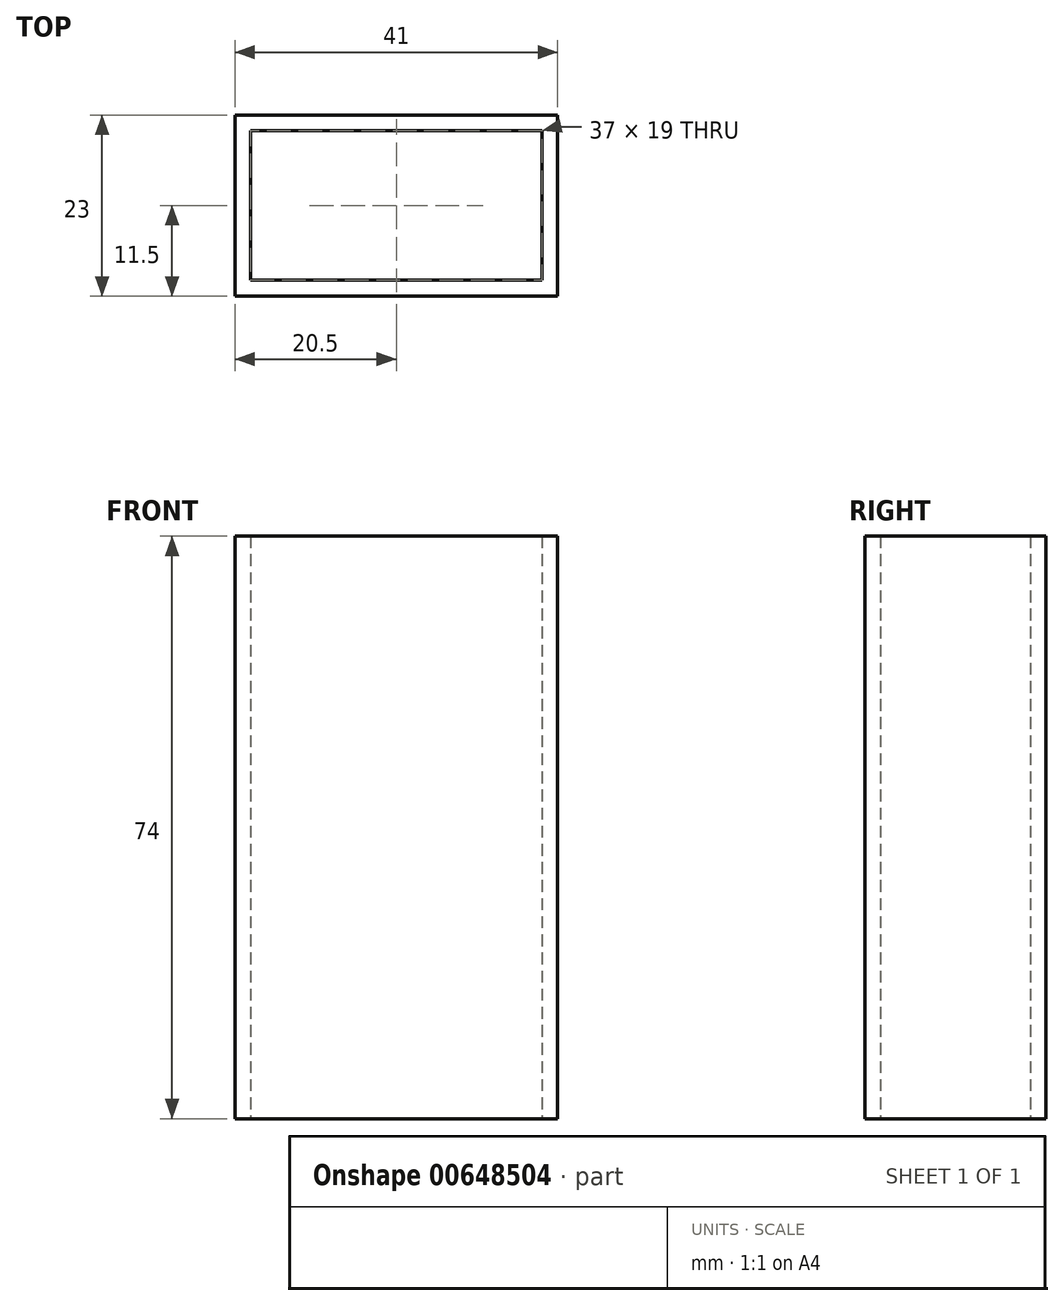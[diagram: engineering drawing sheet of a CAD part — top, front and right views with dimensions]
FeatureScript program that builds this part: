
annotation { "Feature Type Name" : "Feature", "Feature Type Description" : "" }
export const myFeature = defineFeature(function(context is Context, id is Id, definition is map)
    precondition{}
    {
        {
            var Q0;
            Q0=qCreatedBy(makeId("Top.planeOp"),FACE);
            var sketch = newSketch(context, id + "F0", { "sketchPlane" : qUnion([Q0])});
            skLineSegment(sketch, "E0.bottom", {"start": v(20.5, 11.5) * mm, "end": v(-20.5, 11.5) * mm});
            skLineSegment(sketch, "E0.top", {"start": v(20.5, -11.5) * mm, "end": v(-20.5, -11.5) * mm});
            skLineSegment(sketch, "E0.left", {"start": v(20.5, 11.5) * mm, "end": v(20.5, -11.5) * mm});
            skLineSegment(sketch, "E0.right", {"start": v(-20.5, 11.5) * mm, "end": v(-20.5, -11.5) * mm});
            skPoint(sketch, "E0.middle", {"position": v(0, 0) * mm});
            skLineSegment(sketch, "E1.0", {"start": v(18.5, 9.5) * mm, "end": v(-18.5, 9.5) * mm});
            skLineSegment(sketch, "E2.0", {"start": v(-18.5, 9.5) * mm, "end": v(-18.5, -9.5) * mm});
            skLineSegment(sketch, "E3.0", {"start": v(18.5, 9.5) * mm, "end": v(18.5, -9.5) * mm});
            skLineSegment(sketch, "E4.0", {"start": v(18.5, -9.5) * mm, "end": v(-18.5, -9.5) * mm});
            skCircle(sketch, "E5", {"center": v(-9.5, 0) * mm, "radius": 9 * mm});
            skCircle(sketch, "E6", {"center": v(9.5, 0) * mm, "radius": 9 * mm});
            skPoint(sketch, "E7.start.orphan", {"position": v(-18.5, 0) * mm});
            skPoint(sketch, "E8.trimOffspring.end.orphan", {"position": v(18.5, 0) * mm});
            skSolve(sketch);
        }
        {
            var Q0;
            Q0=makeQuery(id+"F0.imprint","IMPRINT",FACE,{"disambiguationData":[TD([[makeQuery(id+"F0.imprint","IMPRINT",EDGE,{"derivedFrom":sQuery(id+"F0.wireOp",EDGE,"E0.bottom")}),1.0]])]});
            extrude(context, id + "F1", {"entities" : qUnion([Q0]), "depth" : 74 * mm, "offsetDistance" : 25 * mm});
        }
    });
